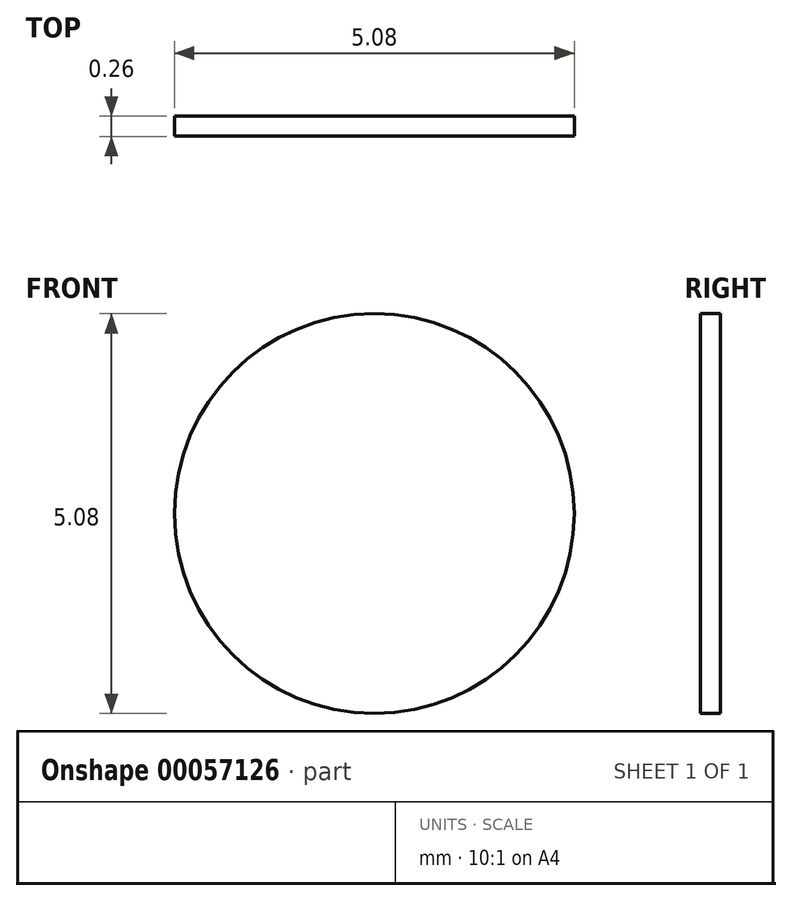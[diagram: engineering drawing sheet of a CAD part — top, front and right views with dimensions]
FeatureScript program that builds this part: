
annotation { "Feature Type Name" : "Feature", "Feature Type Description" : "" }
export const myFeature = defineFeature(function(context is Context, id is Id, definition is map)
    precondition{}
    {
        {
            var Q0;
            Q0=qCreatedBy(makeId("Front.planeOp"),FACE);
            var sketch = newSketch(context, id + "F0", { "sketchPlane" : qUnion([Q0])});
            skCircle(sketch, "E0", {"center": v(0, 0) * mm, "radius": 2.54 * mm});
            skSolve(sketch);
        }
        {
            var Q0;
            Q0=makeQuery(id+"F0.imprint","IMPRINT",FACE,{"disambiguationData":[TD([[makeQuery(id+"F0.imprint","IMPRINT",EDGE,{"derivedFrom":sQuery(id+"F0.wireOp",EDGE,"E0")}),1.0]])]});
            extrude(context, id + "F1", {"entities" : qUnion([Q0]), "depth" : 0.25 * mm, "symmetric" : true});
        }
    });
